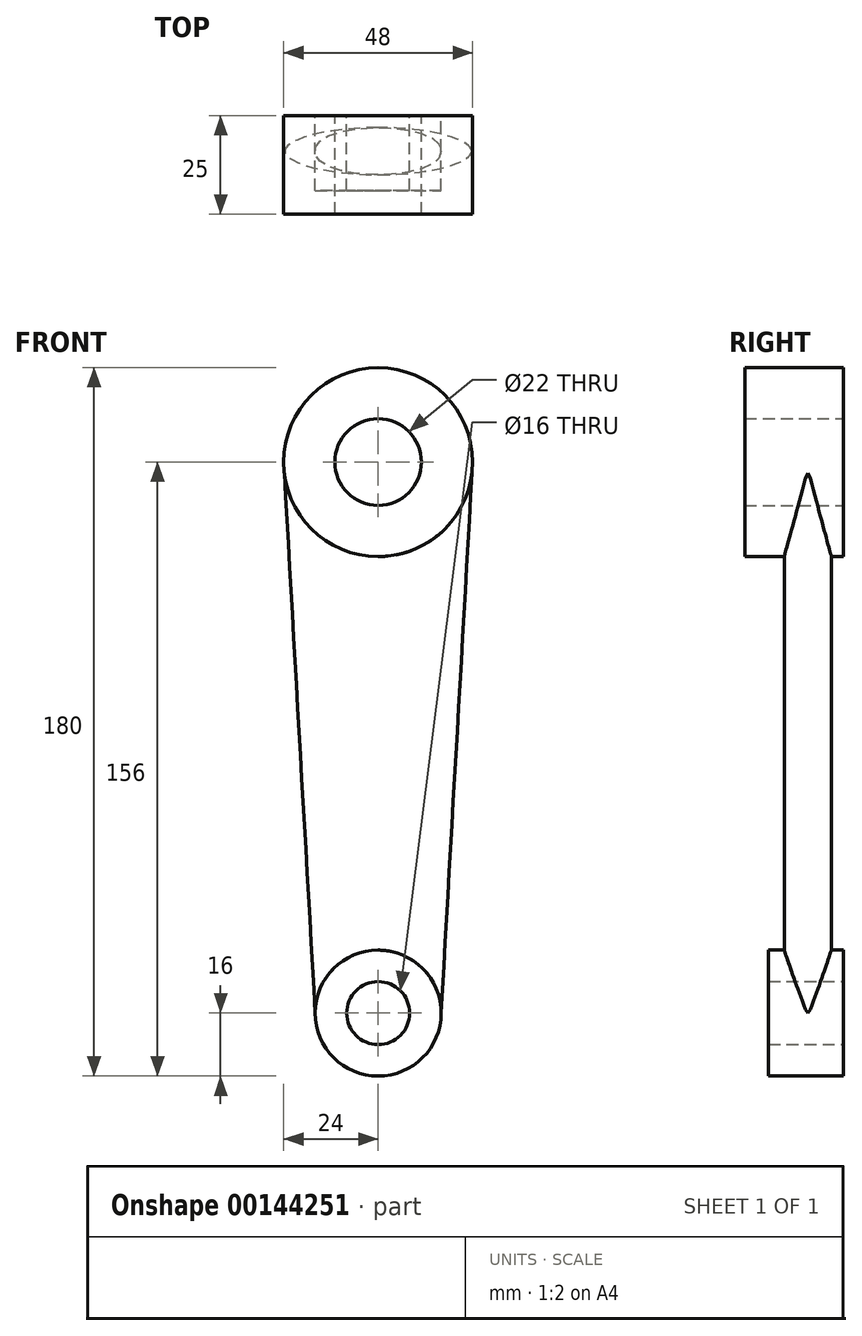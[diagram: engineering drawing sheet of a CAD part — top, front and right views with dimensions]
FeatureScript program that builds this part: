
annotation { "Feature Type Name" : "Feature", "Feature Type Description" : "" }
export const myFeature = defineFeature(function(context is Context, id is Id, definition is map)
    precondition{}
    {
        {
            var Q0;
            Q0=qCreatedBy(makeId("Front.planeOp"),FACE);
            var sketch = newSketch(context, id + "F0", { "sketchPlane" : qUnion([Q0])});
            skCircle(sketch, "E0", {"center": v(0, 0) * mm, "radius": 8 * mm});
            skCircle(sketch, "E1", {"center": v(0, 0) * mm, "radius": 16 * mm});
            skCircle(sketch, "E2", {"center": v(0, 140) * mm, "radius": 11 * mm});
            skCircle(sketch, "E3", {"center": v(0, 140) * mm, "radius": 24 * mm});
            skSolve(sketch);
        }
        {
            var Q0;
            Q0=makeQuery(id+"F0.imprint","IMPRINT",FACE,{"disambiguationData":[TD([[makeQuery(id+"F0.imprint","IMPRINT",EDGE,{"derivedFrom":sQuery(id+"F0.wireOp",EDGE,"E0")}),-1.0]])]});
            var Q1;
            Q1=makeQuery(id+"F0.imprint","IMPRINT",FACE,{"disambiguationData":[TD([[makeQuery(id+"F0.imprint","IMPRINT",EDGE,{"derivedFrom":sQuery(id+"F0.wireOp",EDGE,"E0")}),1.0]])]});
            extrude(context, id + "F1", {"entities" : qUnion([Q0, Q1]), "depth" : 19 * mm});
        }
        {
            var Q0;
            Q0=makeQuery(id+"F0.imprint","IMPRINT",FACE,{"disambiguationData":[TD([[makeQuery(id+"F0.imprint","IMPRINT",EDGE,{"derivedFrom":sQuery(id+"F0.wireOp",EDGE,"E2")}),-1.0]])]});
            var Q1;
            Q1=makeQuery(id+"F0.imprint","IMPRINT",FACE,{"disambiguationData":[TD([[makeQuery(id+"F0.imprint","IMPRINT",EDGE,{"derivedFrom":sQuery(id+"F0.wireOp",EDGE,"E2")}),1.0]])]});
            extrude(context, id + "F2", {"entities" : qUnion([Q0, Q1]), "depth" : 25 * mm});
        }
        {
            var Q0;
            Q0=qCreatedBy(makeId("Top.planeOp"),FACE);
            var sketch = newSketch(context, id + "F3", { "sketchPlane" : qUnion([Q0])});
            skEllipse(sketch, "E4", {"center": v(0, -9) * mm, "majorRadius": 16 * mm, "minorRadius": 6 * mm, "majorAxis": v(1, 0)});
            skPoint(sketch, "E5", {"position": v(0, -3) * mm});
            skLineSegment(sketch, "E6", {"start": v(16, 0) * mm, "end": v(16, -19) * mm, "construction": true});
            skSolve(sketch);
        }
        {
            var Q0;
            Q0=sQuery(id+"F0.wireOp",VERTEX,"E3.center");
            var Q1;
            Q1=qCreatedBy(makeId("Top.planeOp"),FACE);
            cPlane(context, id + "F4", {"entities" : qUnion([Q0, Q1]), "cplaneType" : CPlaneType.PLANE_POINT, "offset" : 25 * mm, "width" : 150 * mm, "height" : 150 * mm});
        }
        {
            var Q0;
            Q0=qCreatedBy(id+"F4.planeOp",FACE);
            var sketch = newSketch(context, id + "F5", { "sketchPlane" : qUnion([Q0])});
            skEllipse(sketch, "E7", {"center": v(0, -9) * mm, "majorRadius": 24 * mm, "minorRadius": 6 * mm, "majorAxis": v(1, 0)});
            skLineSegment(sketch, "E8", {"start": v(24, 0) * mm, "end": v(24, -25) * mm, "construction": true});
            skSolve(sketch);
        }
        {
            var Q2;
            Q2=makeQuery(id+"F5.imprint","IMPRINT",FACE,{"disambiguationData":[TD([[makeQuery(id+"F5.imprint","IMPRINT",EDGE,{"derivedFrom":sQuery(id+"F5.wireOp",EDGE,"E7")}),1.0]])]});
            var Q3;
            Q3=makeQuery(id+"F3.imprint","IMPRINT",FACE,{"disambiguationData":[TD([[makeQuery(id+"F3.imprint","IMPRINT",EDGE,{"derivedFrom":sQuery(id+"F3.wireOp",EDGE,"E4")}),1.0]])]});
            loft(context, id + "F6", {"operationType" : NewBodyOperationType.ADD, "sheetProfilesArray" : [{ "sheetProfileEntities" : qUnion([Q2]) }, { "sheetProfileEntities" : qUnion([Q3]) }]});
        }
        {
            var Q0;
            Q0=makeQuery(id+"F0.imprint","IMPRINT",FACE,{"disambiguationData":[TD([[makeQuery(id+"F0.imprint","IMPRINT",EDGE,{"derivedFrom":sQuery(id+"F0.wireOp",EDGE,"E2")}),1.0]])]});
            var Q1;
            Q1=makeQuery(id+"F0.imprint","IMPRINT",FACE,{"disambiguationData":[TD([[makeQuery(id+"F0.imprint","IMPRINT",EDGE,{"derivedFrom":sQuery(id+"F0.wireOp",EDGE,"E0")}),1.0]])]});
            extrude(context, id + "F7", {"entities" : qUnion([Q0, Q1]), "operationType" : NewBodyOperationType.REMOVE, "endBound" : BoundingType.THROUGH_ALL, "depth" : 25 * mm});
        }
        {
            var Q0;
            Q0=makeQuery(id+"F1.opExtrude","SWEPT_BODY",BODY,{"disambiguationData":[OSD([sQuery(id+"F0.wireOp",EDGE,"E1")])]});
            transform(context, id + "F8", {"entities" : qUnion([Q0]), "transformType" : TransformType.TRANSLATION_3D, "dx" : 0 * mm, "dy" : 0 * mm, "dz" : 0 * mm, "makeCopy" : true});
        }
        {
            var Q0;
            Q0=makeQuery(id+"F8.opPattern","COPY",BODY,{"derivedFrom":makeQuery(id+"F1.opExtrude","SWEPT_BODY",BODY,{"disambiguationData":[OSD([sQuery(id+"F0.wireOp",EDGE,"E1")])]}),"instanceName":"1"});
            deleteBodies(context, id + "F9", {"entities" : qUnion([Q0])});
        }
        {
            var Q0;
            Q0=makeQuery(id+"F1.opExtrude","SWEPT_BODY",BODY,{"disambiguationData":[OSD([sQuery(id+"F0.wireOp",EDGE,"E1")])]});
            transform(context, id + "F10", {"entities" : qUnion([Q0]), "transformType" : TransformType.TRANSLATION_3D, "dx" : 0 * mm, "dy" : 0 * mm, "dz" : 0 * mm, "makeCopy" : true});
        }
        {
            var Q0;
            Q0=makeQuery(id+"F10.opPattern","COPY",BODY,{"derivedFrom":makeQuery(id+"F1.opExtrude","SWEPT_BODY",BODY,{"disambiguationData":[OSD([sQuery(id+"F0.wireOp",EDGE,"E1")])]}),"instanceName":"1"});
            deleteBodies(context, id + "F11", {"entities" : qUnion([Q0])});
        }
    });
